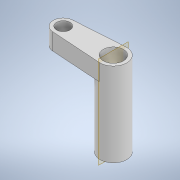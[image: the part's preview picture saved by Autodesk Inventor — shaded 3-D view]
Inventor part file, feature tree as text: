
AUTODESK INVENTOR PART (.ipt)
format: ipt  version: 2020 (Build 240168000, 168)  size: 135,680 bytes
history: native  units: in
note: dims shown in document units (in); Inventor stores cm internally (conversion verified against a paired STEP export)
features: sketch x5, extrude x4, hole x1
ambient origin geometry x8: Origin, YZ Plane, XZ Plane, XY Plane, X Axis, Y Axis, Z Axis, Center Point
bodies: Solid1 (feature_tree)
feature tree (10):
  extrude  "Extrusion1"  Depth=0.9843in TaperAngle=0.0deg
  extrude  "Extrusion2"  Depth=0.5118in TaperAngle=0.0deg
  extrude  "Extrusion3"  Depth=0.1575in
  extrude  "Extrusion4"  Depth=0.9843in
  hole  "Hole1"  [1 undecoded]
  sketch  "Sketch1"  dims[d0=0.315in d1=0.9843in d2=0.0in]
  sketch  "Sketch2"  dims[d3=0.2362in d4=0.5118in d5=0.0in]
  sketch  "Sketch3"  dims[d8=0.1575in d9=0.1575in]
  sketch  "Sketch4"  dims[d10=0.9843in d11=0.0in d12=0.2362in]
  sketch  "Sketch5"  dims[d13=0.1969in d14=0.0in d15=0.1575in d16=0.1575in d17=0.2362in d18=0.2559in d19=0.1575in d20=90.0deg d21=0.315in d22=0.8108in]
note: 1 required parameter value undecoded (feature->parameter linkage not recoverable at this tier; creation-order binding heuristic only, values carry confidence <= 0.55)
